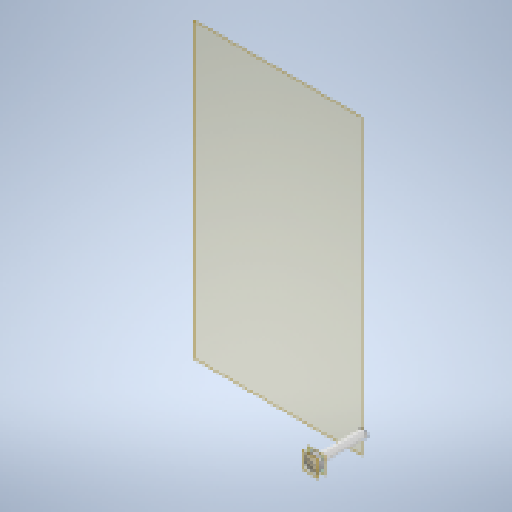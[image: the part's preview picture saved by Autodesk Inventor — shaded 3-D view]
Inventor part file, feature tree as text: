
AUTODESK INVENTOR PART (.ipt)
format: ipt  version: 2023 (Build 270158000, 158)  size: 153,088 bytes
history: native  units: mm
features: other x5, plane x3, sketch x3, extrude x2, loft x1, reference x1, projected_geometry x1
ambient origin geometry x8: Origin, YZ Plane, XZ Plane, XY Plane, X Axis, Y Axis, Z Axis, Center Point
bodies: Solid1 (feature_tree)
feature tree (16):
  plane  "Work Plane1"
  extrude  "Extrusion1"  Depth=17.9mm TaperAngle=0.0deg
  extrude  "Extrusion2"  Depth=1.35mm TaperAngle=0.0deg
  plane  "Work Plane2"
  loft  "Loft1"
  plane  "Work Plane3"
  sketch  "Sketch1"  dims[d1=2.9mm d2=17.9mm d3=0.0mm]
  reference  "Reference1"
  sketch  "Sketch2"  dims[d4=5.83mm d5=1.35mm d6=0.0mm]
  projected_geometry  "Projected Loop1"
  sketch  "Sketch3"  dims[d7=1.01mm d8=0.0mm d9=90.0deg d10=0.0mm d11=90.0deg d12=0.0mm]
  other  "Edges1"
  parser-record x1  (decoder bookkeeping rows leaked as tree rows — omitted from the tree; the rows remain in map.json)
  other  "doorLockAssembly_V4.iam"
  other  "housingFront:1"
  other  "housingPlate:1"
note: 1 file-system path scrubbed to <path> (originals preserved in map.json)
